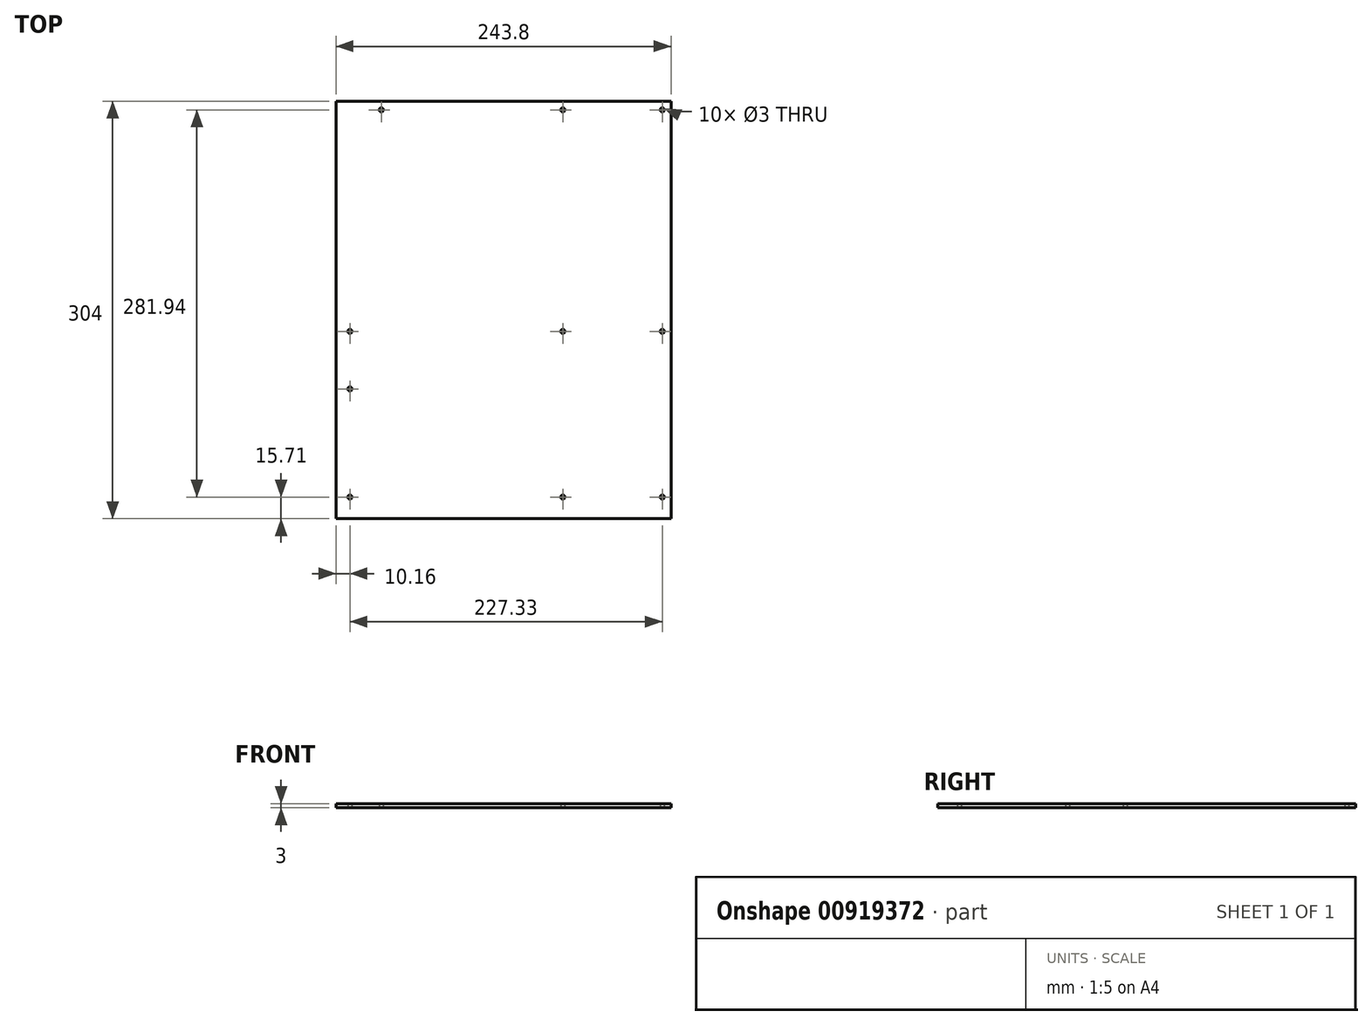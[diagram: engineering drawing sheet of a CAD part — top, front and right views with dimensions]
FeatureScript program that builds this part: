
annotation { "Feature Type Name" : "Feature", "Feature Type Description" : "" }
export const myFeature = defineFeature(function(context is Context, id is Id, definition is map)
    precondition{}
    {
        {
            var Q0;
            Q0=qCreatedBy(makeId("Top.planeOp"),FACE);
            var sketch = newSketch(context, id + "F0", { "sketchPlane" : qUnion([Q0])});
            skLineSegment(sketch, "E0.bottom", {"start": v(121.9, 152) * mm, "end": v(-121.9, 152) * mm});
            skLineSegment(sketch, "E0.top", {"start": v(121.9, -152) * mm, "end": v(-121.9, -152) * mm});
            skLineSegment(sketch, "E0.left", {"start": v(121.9, 152) * mm, "end": v(121.9, -152) * mm});
            skLineSegment(sketch, "E0.right", {"start": v(-121.9, 152) * mm, "end": v(-121.9, -152) * mm});
            skPoint(sketch, "E0.middle", {"position": v(0, 0) * mm});
            skCircle(sketch, "E1", {"center": v(115.59, 145.65) * mm, "radius": 1.5 * mm});
            skCircle(sketch, "E2", {"center": v(115.6, -15.64) * mm, "radius": 1.5 * mm});
            skCircle(sketch, "E3", {"center": v(115.6, -136.3) * mm, "radius": 1.5 * mm});
            skLineSegment(sketch, "E4", {"start": v(0, -152) * mm, "end": v(0, 152) * mm, "construction": true});
            skLineSegment(sketch, "E5", {"start": v(121.9, 0) * mm, "end": v(-121.9, 0) * mm, "construction": true});
            skCircle(sketch, "E6", {"center": v(-88.88, 145.65) * mm, "radius": 1.5 * mm});
            skCircle(sketch, "E7", {"center": v(43.2, 145.65) * mm, "radius": 1.5 * mm});
            skCircle(sketch, "E8", {"center": v(-111.74, -15.64) * mm, "radius": 1.5 * mm});
            skCircle(sketch, "E9", {"center": v(-111.74, -57.55) * mm, "radius": 1.5 * mm});
            skCircle(sketch, "E10", {"center": v(-111.74, -136.29) * mm, "radius": 1.5 * mm});
            skCircle(sketch, "E11", {"center": v(43.2, -15.64) * mm, "radius": 1.5 * mm});
            skCircle(sketch, "E12", {"center": v(43.2, -136.29) * mm, "radius": 1.5 * mm});
            skSolve(sketch);
        }
        {
            var Q0;
            Q0 = qSketchRegion(id + "F0", true);
            extrude(context, id + "F1", {"entities" : qUnion([Q0]), "depth" : 3 * mm, "offsetDistance" : 25 * mm});
        }
    });
